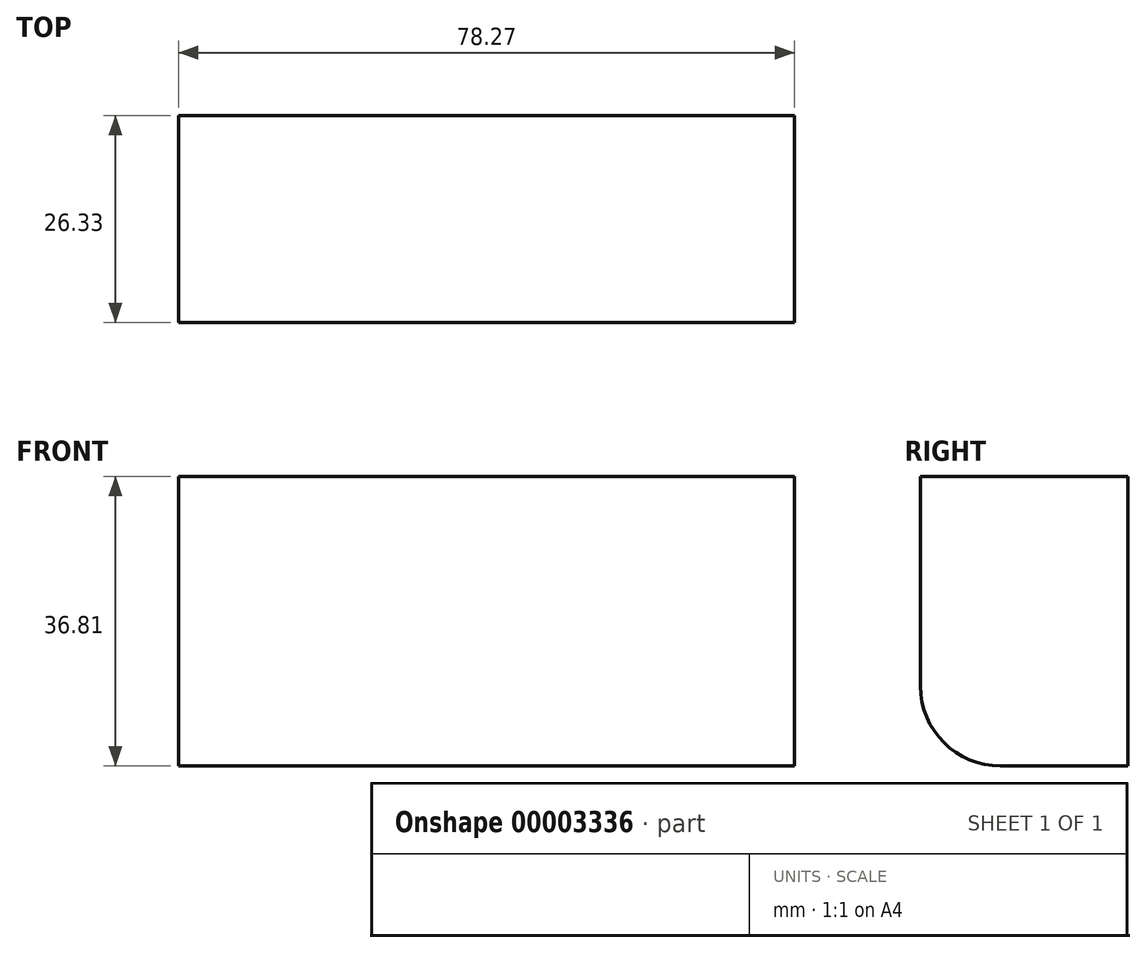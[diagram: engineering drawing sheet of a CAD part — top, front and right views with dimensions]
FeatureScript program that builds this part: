
annotation { "Feature Type Name" : "Feature", "Feature Type Description" : "" }
export const myFeature = defineFeature(function(context is Context, id is Id, definition is map)
    precondition{}
    {
        {
            var Q0;
            Q0=qCreatedBy(makeId("Front.planeOp"),FACE);
            var sketch = newSketch(context, id + "F0", { "sketchPlane" : qUnion([Q0])});
            skLineSegment(sketch, "E0.bottom", {"start": v(-35.08, 19.71) * mm, "end": v(43.2, 19.71) * mm});
            skLineSegment(sketch, "E0.top", {"start": v(-35.08, -17.1) * mm, "end": v(43.2, -17.1) * mm});
            skLineSegment(sketch, "E0.left", {"start": v(-35.08, 19.71) * mm, "end": v(-35.08, -17.1) * mm});
            skLineSegment(sketch, "E0.right", {"start": v(43.2, 19.71) * mm, "end": v(43.2, -17.1) * mm});
            skSolve(sketch);
        }
        {
            var Q0;
            Q0=makeQuery(id+"F0.imprint","IMPRINT",FACE,{"disambiguationData":[TD([[makeQuery(id+"F0.imprint","IMPRINT",EDGE,{"derivedFrom":sQuery(id+"F0.wireOp",EDGE,"E0.bottom")}),-1.0]])]});
            extrude(context, id + "F1", {"entities" : qUnion([Q0]), "depth" : 26.33 * mm});
        }
        {
            var Q0;
            Q0=makeQuery(id+"F1.opExtrude","CAP_EDGE",EDGE,{"disambiguationData":[OSD([sQuery(id+"F0.wireOp",EDGE,"E0.top")])],"isStart":false});
            fillet(context, id + "F2", {"entities" : qUnion([Q0]), "radius" : 10.16 * mm, "tangentPropagation" : true, "allowEdgeOverflow" : false});
        }
    });
